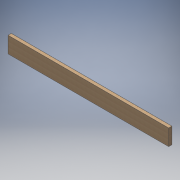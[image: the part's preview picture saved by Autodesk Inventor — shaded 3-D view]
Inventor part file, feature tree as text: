
AUTODESK INVENTOR PART (.ipt)
format: ipt  version: 2019 (Build 230136000, 136)  size: 123,904 bytes
history: native  units: mm
features: other x7, reference x2, extrude x1, sketch x1
ambient origin geometry x8: Origin, YZ Plane, XZ Plane, XY Plane, X Axis, Y Axis, Z Axis, Center Point
bodies: Body1 (feature_tree)
feature tree (11):
  other  "Твердое тело1"
  extrude  "Выдавливание1"  Depth=40.0mm TaperAngle=0.0deg
  sketch  "Эскиз1"
  reference  "Ссылка2"
  reference  "Ссылка3"
  other  "<userpath>\Documents\Inventor\Мурзин\Лестница.iam"
  other  "Лестница.iam"
  other  "Марш-02:2"
  other  "Косоур-02:3"
  other  "Марш-01:1"
  other  "Косоур-01:1"
